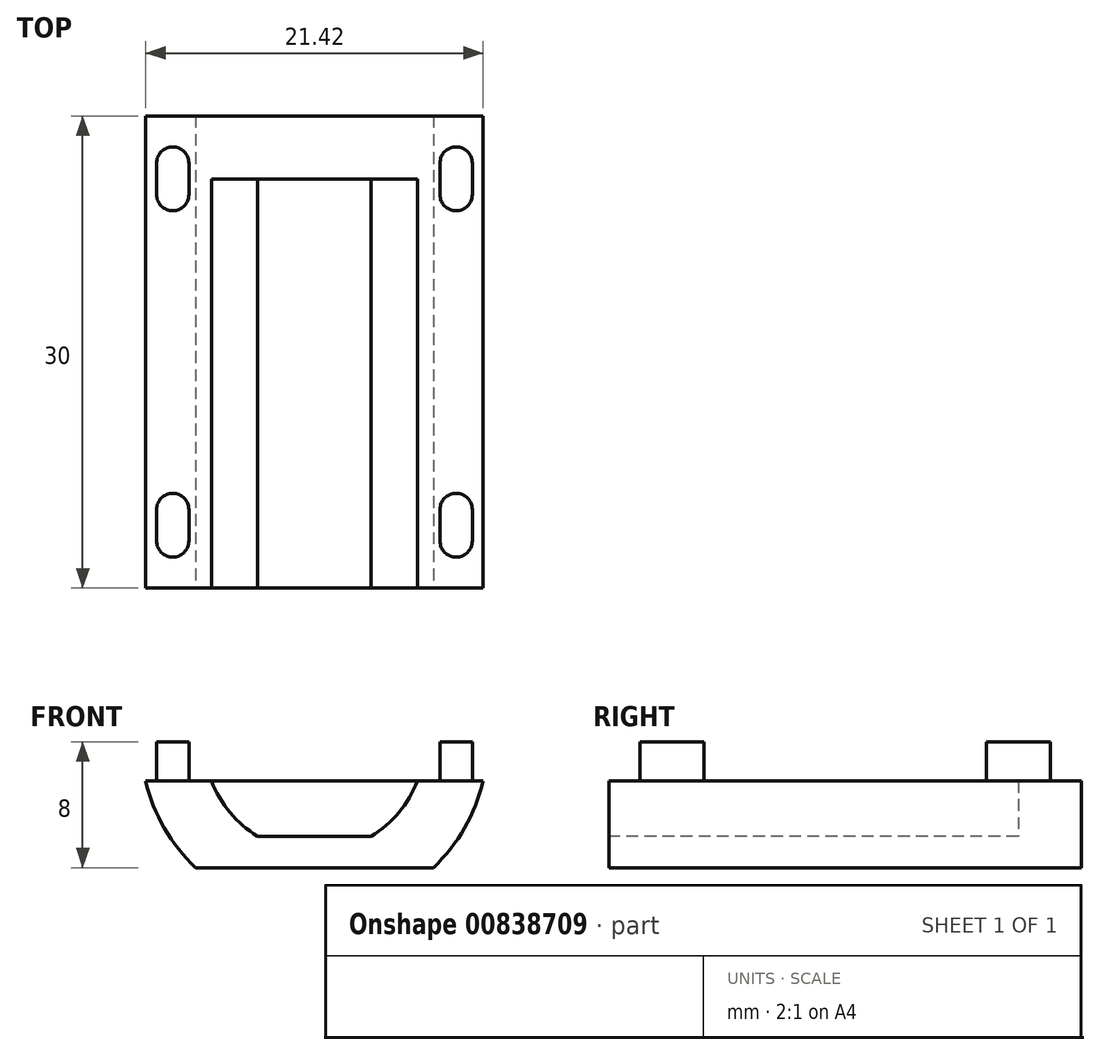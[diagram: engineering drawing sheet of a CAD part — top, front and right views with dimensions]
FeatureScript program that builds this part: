
annotation { "Feature Type Name" : "Feature", "Feature Type Description" : "" }
export const myFeature = defineFeature(function(context is Context, id is Id, definition is map)
    precondition{}
    {
        {
            var Q0;
            Q0=qCreatedBy(makeId("Top.planeOp"),FACE);
            var sketch = newSketch(context, id + "F0", { "sketchPlane" : qUnion([Q0])});
            skLineSegment(sketch, "E0", {"start": v(0, 41.82) * mm, "end": v(0, -8.8) * mm, "construction": true});
            skSolve(sketch);
        }
        {
            var Q0;
            Q0=qCreatedBy(makeId("Top.planeOp"),FACE);
            var sketch = newSketch(context, id + "F1", { "sketchPlane" : qUnion([Q0])});
            skLineSegment(sketch, "E1.bottom", {"start": v(-11, 30) * mm, "end": v(11, 30) * mm});
            skLineSegment(sketch, "E1.top", {"start": v(-11, 0) * mm, "end": v(11, 0) * mm});
            skLineSegment(sketch, "E1.left", {"start": v(-11, 30) * mm, "end": v(-11, 0) * mm});
            skLineSegment(sketch, "E1.right", {"start": v(11, 30) * mm, "end": v(11, 0) * mm});
            skSolve(sketch);
        }
        {
            var Q0;
            Q0=makeQuery(id+"F1.imprint","IMPRINT",FACE,{"disambiguationData":[TD([[makeQuery(id+"F1.imprint","IMPRINT",EDGE,{"derivedFrom":sQuery(id+"F1.wireOp",EDGE,"E1.bottom")}),-1.0]])]});
            extrude(context, id + "F2", {"entities" : qUnion([Q0]), "oppositeDirection" : true, "depth" : 8 * mm, "offsetDistance" : 25 * mm});
        }
        {
            var Q0;
            Q0=makeQuery(id+"F2.opExtrude","SWEPT_FACE",FACE,{"disambiguationData":[OSD([sQuery(id+"F1.wireOp",EDGE,"E1.top")])]});
            var sketch = newSketch(context, id + "F3", { "sketchPlane" : qUnion([Q0])});
            skCircle(sketch, "E2", {"center": v(0, 0) * mm, "radius": 11 * mm});
            skLineSegment(sketch, "E3", {"start": v(-11, 0) * mm, "end": v(-11, -8) * mm});
            skLineSegment(sketch, "E4", {"start": v(-11, -8) * mm, "end": v(-7.55, -8) * mm});
            skLineSegment(sketch, "E5", {"start": v(11, 0) * mm, "end": v(11, -8) * mm});
            skLineSegment(sketch, "E6", {"start": v(11, -8) * mm, "end": v(7.55, -8) * mm});
            skSolve(sketch);
        }
        {
            var Q0;
            {var subQ0=sQuery(id+"F3.wireOp",EDGE,"E5");Q0=makeQuery(id+"F3.imprint","IMPRINT",FACE,{"disambiguationData":[TD([[makeQuery(id+"F3.imprint","IMPRINT",EDGE,{"derivedFrom":subQ0}),1.0]])]});}
            var Q1;
            {var subQ0=sQuery(id+"F3.wireOp",EDGE,"E3");Q1=makeQuery(id+"F3.imprint","IMPRINT",FACE,{"disambiguationData":[TD([[makeQuery(id+"F3.imprint","IMPRINT",EDGE,{"derivedFrom":subQ0}),-1.0]])]});}
            extrude(context, id + "F4", {"entities" : qUnion([Q0, Q1]), "operationType" : NewBodyOperationType.REMOVE, "endBound" : BoundingType.THROUGH_ALL, "oppositeDirection" : true, "depth" : 25 * mm, "offsetDistance" : 25 * mm});
        }
        {
            var Q0;
            Q0=makeQuery(id+"F2.opExtrude","CAP_FACE",FACE,{"disambiguationData":[OSD([sQuery(id+"F1.wireOp",EDGE,"E1.bottom"),sQuery(id+"F1.wireOp",EDGE,"E1.top"),sQuery(id+"F1.wireOp",EDGE,"E1.left"),sQuery(id+"F1.wireOp",EDGE,"E1.right")])],"isStart":true});
            var sketch = newSketch(context, id + "F5", { "sketchPlane" : qUnion([Q0])});
            skLineSegment(sketch, "E7", {"start": v(-9, 5) * mm, "end": v(-9, 3) * mm});
            skLineSegment(sketch, "E8", {"start": v(9, 5) * mm, "end": v(9, 3) * mm});
            skArc(sketch, "E9.0.startCap", {"start": v(-10.02, 5) * mm, "mid": v(-9, 6.03) * mm, "end": v(-7.97, 5) * mm});
            skArc(sketch, "E9.0.endCap", {"start": v(-7.98, 3) * mm, "mid": v(-9, 1.98) * mm, "end": v(-10.03, 3) * mm});
            skLineSegment(sketch, "E9.0.left", {"start": v(-7.98, 5) * mm, "end": v(-7.98, 3) * mm});
            skLineSegment(sketch, "E9.0.right", {"start": v(-10.02, 5) * mm, "end": v(-10.02, 3) * mm});
            skArc(sketch, "E10.0.startCap", {"start": v(7.97, 5) * mm, "mid": v(9, 6.03) * mm, "end": v(10.02, 5) * mm});
            skArc(sketch, "E10.0.endCap", {"start": v(10.03, 3) * mm, "mid": v(9, 1.98) * mm, "end": v(7.98, 3) * mm});
            skLineSegment(sketch, "E10.0.left", {"start": v(10.02, 5) * mm, "end": v(10.02, 3) * mm});
            skLineSegment(sketch, "E10.0.right", {"start": v(7.98, 5) * mm, "end": v(7.98, 3) * mm});
            skLineSegment(sketch, "E11", {"start": v(-9, 27) * mm, "end": v(-9, 25) * mm});
            skLineSegment(sketch, "E12", {"start": v(9, 27) * mm, "end": v(9, 25) * mm});
            skArc(sketch, "E13.0.startCap", {"start": v(-10.03, 27) * mm, "mid": v(-9, 28.03) * mm, "end": v(-7.98, 27) * mm});
            skArc(sketch, "E13.0.endCap", {"start": v(-7.98, 25) * mm, "mid": v(-9, 23.98) * mm, "end": v(-10.03, 25) * mm});
            skLineSegment(sketch, "E13.0.left", {"start": v(-7.98, 27) * mm, "end": v(-7.98, 25) * mm});
            skLineSegment(sketch, "E13.0.right", {"start": v(-10.03, 27) * mm, "end": v(-10.03, 25) * mm});
            skArc(sketch, "E14.0.startCap", {"start": v(7.98, 27) * mm, "mid": v(9, 28.03) * mm, "end": v(10.03, 27) * mm});
            skArc(sketch, "E14.0.endCap", {"start": v(10.03, 25) * mm, "mid": v(9, 23.98) * mm, "end": v(7.98, 25) * mm});
            skLineSegment(sketch, "E14.0.left", {"start": v(10.03, 27) * mm, "end": v(10.03, 25) * mm});
            skLineSegment(sketch, "E14.0.right", {"start": v(7.98, 27) * mm, "end": v(7.98, 25) * mm});
            skSolve(sketch);
        }
        {
            var Q0;
            Q0=makeQuery(id+"F5.imprint","IMPRINT",FACE,{"disambiguationData":[TD([[makeQuery(id+"F5.imprint","IMPRINT",EDGE,{"derivedFrom":sQuery(id+"F5.wireOp",EDGE,"E9.0.startCap")}),-1.0]])]});
            var Q1;
            Q1=makeQuery(id+"F5.imprint","IMPRINT",FACE,{"disambiguationData":[TD([[makeQuery(id+"F5.imprint","IMPRINT",EDGE,{"derivedFrom":sQuery(id+"F5.wireOp",EDGE,"E10.0.startCap")}),-1.0]])]});
            var Q2;
            Q2=makeQuery(id+"F5.imprint","IMPRINT",FACE,{"disambiguationData":[TD([[makeQuery(id+"F5.imprint","IMPRINT",EDGE,{"derivedFrom":sQuery(id+"F5.wireOp",EDGE,"E13.0.startCap")}),-1.0]])]});
            var Q3;
            Q3=makeQuery(id+"F5.imprint","IMPRINT",FACE,{"disambiguationData":[TD([[makeQuery(id+"F5.imprint","IMPRINT",EDGE,{"derivedFrom":sQuery(id+"F5.wireOp",EDGE,"E14.0.startCap")}),-1.0]])]});
            extrude(context, id + "F6", {"entities" : qUnion([Q0, Q1, Q2, Q3]), "operationType" : NewBodyOperationType.REMOVE, "oppositeDirection" : true, "depth" : 2.5 * mm, "offsetDistance" : 25 * mm});
        }
        {
            var Q0;
            Q0=makeQuery(id+"F2.opExtrude","SWEPT_FACE",FACE,{"disambiguationData":[OSD([sQuery(id+"F1.wireOp",EDGE,"E1.top")])]});
            var sketch = newSketch(context, id + "F7", { "sketchPlane" : qUnion([Q0])});
            skArc(sketch, "E15", {"start": v(-7, 0) * mm, "mid": v(-6.1, -3.45) * mm, "end": v(-3.6, -6) * mm});
            skLineSegment(sketch, "E16", {"start": v(-7, 0) * mm, "end": v(7, 0) * mm});
            skLineSegment(sketch, "E17", {"start": v(-3.6, -6) * mm, "end": v(3.6, -6) * mm});
            skArc(sketch, "E18.trimOffspring", {"start": v(3.6, -6) * mm, "mid": v(6.1, -3.45) * mm, "end": v(7, 0) * mm});
            skSolve(sketch);
        }
        {
            var Q0;
            Q0=makeQuery(id+"F7.imprint","IMPRINT",FACE,{"disambiguationData":[TD([[makeQuery(id+"F7.imprint","IMPRINT",EDGE,{"derivedFrom":sQuery(id+"F7.wireOp",EDGE,"E15")}),1.0]])]});
            extrude(context, id + "F8", {"entities" : qUnion([Q0]), "operationType" : NewBodyOperationType.REMOVE, "oppositeDirection" : true, "depth" : 26 * mm, "offsetDistance" : 25 * mm});
        }
        {
            var Q0;
            Q0=makeQuery(id+"F8.boolean.opBoolean","COPY",FACE,{"derivedFrom":makeQuery(id+"F8.opExtrude","CAP_FACE",FACE,{"disambiguationData":[OSD([sQuery(id+"F7.wireOp",EDGE,"E15"),sQuery(id+"F7.wireOp",EDGE,"E16"),sQuery(id+"F7.wireOp",EDGE,"E17"),sQuery(id+"F7.wireOp",EDGE,"E18.trimOffspring")])],"isStart":false})});
            var sketch = newSketch(context, id + "F9", { "sketchPlane" : qUnion([Q0])});
            skLineSegment(sketch, "E19.bottom", {"start": v(-1.5, 0) * mm, "end": v(1.5, 0) * mm});
            skLineSegment(sketch, "E19.top", {"start": v(-1.5, -1.5) * mm, "end": v(1.5, -1.5) * mm});
            skLineSegment(sketch, "E19.left", {"start": v(-1.5, 0) * mm, "end": v(-1.5, -1.5) * mm});
            skLineSegment(sketch, "E19.right", {"start": v(1.5, 0) * mm, "end": v(1.5, -1.5) * mm});
            skSolve(sketch);
        }
        {
            var Q0;
            Q0=makeQuery(id+"F9.imprint","IMPRINT",FACE,{"disambiguationData":[TD([[makeQuery(id+"F9.imprint","IMPRINT",EDGE,{"derivedFrom":sQuery(id+"F9.wireOp",EDGE,"E19.bottom")}),-1.0]])]});
            extrude(context, id + "F10", {"entities" : qUnion([Q0]), "operationType" : NewBodyOperationType.REMOVE, "oppositeDirection" : true, "depth" : 3 * mm, "offsetDistance" : 25 * mm});
        }
    });
